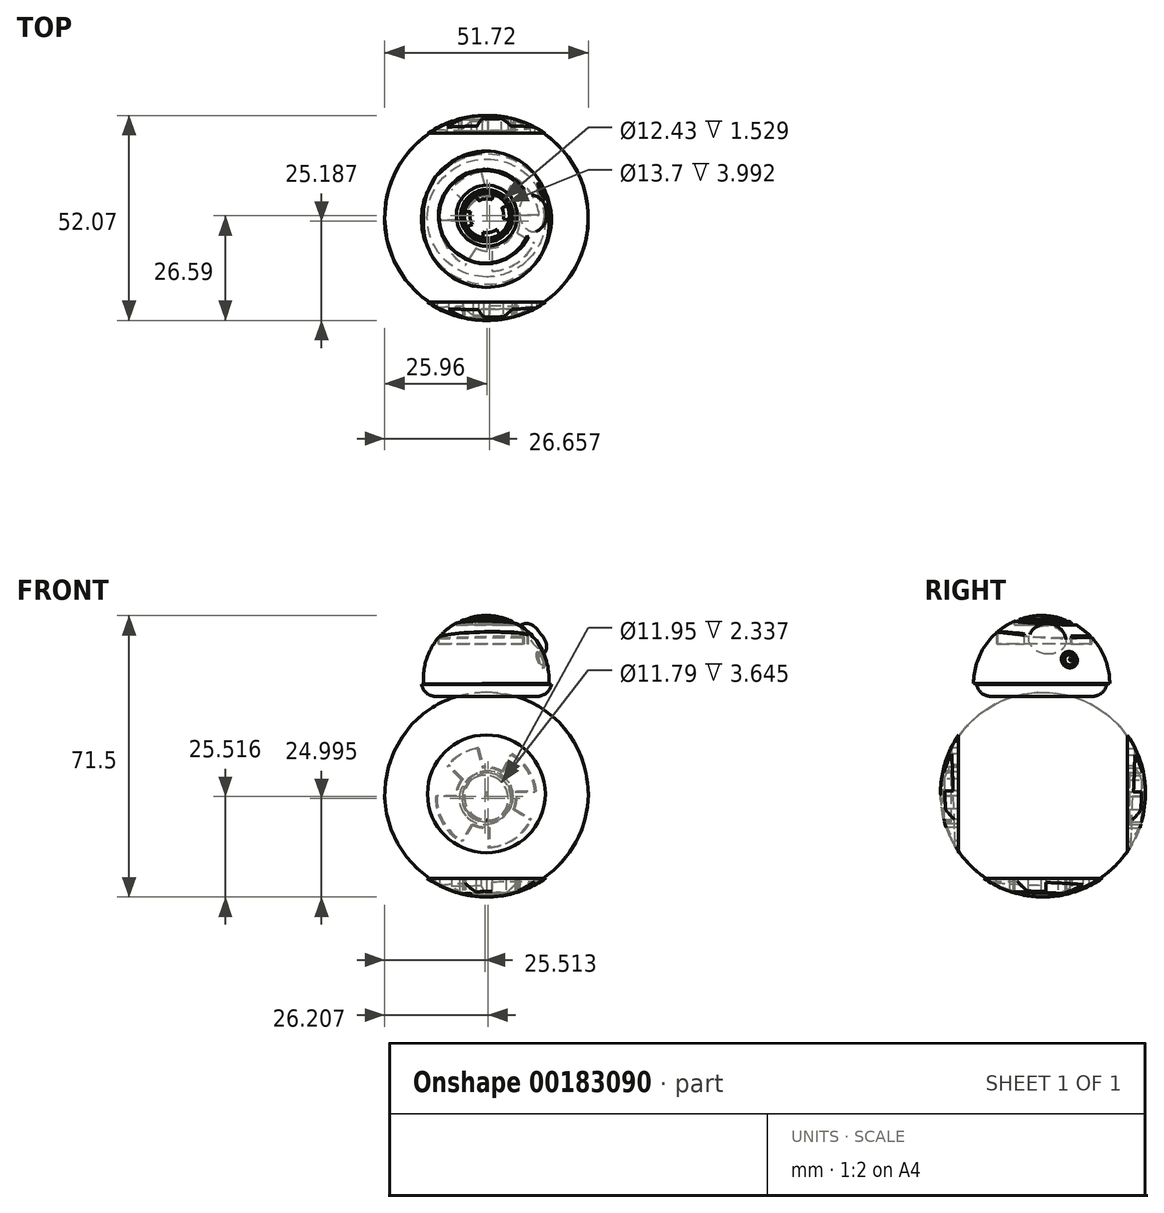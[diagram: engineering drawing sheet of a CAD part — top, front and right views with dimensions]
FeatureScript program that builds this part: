
annotation { "Feature Type Name" : "Feature", "Feature Type Description" : "" }
export const myFeature = defineFeature(function(context is Context, id is Id, definition is map)
    precondition{}
    {
        {
            var Q0;
            Q0=qCreatedBy(makeId("Right.planeOp"),FACE);
            var sketch = newSketch(context, id + "F0", { "sketchPlane" : qUnion([Q0])});
            skArc(sketch, "E0", {"start": v(-25.69, 0) * mm, "mid": v(0.35, -26.2) * mm, "end": v(26.38, 0) * mm});
            skLineSegment(sketch, "E1", {"start": v(-25.69, 0) * mm, "end": v(26.38, 0) * mm});
            skSolve(sketch);
        }
        {
            var Q0;
            Q0=makeQuery(id+"F0.imprint","IMPRINT",FACE,{"disambiguationData":[TD([[makeQuery(id+"F0.imprint","IMPRINT",EDGE,{"derivedFrom":sQuery(id+"F0.wireOp",EDGE,"E0")}),1.0]])]});
            var Q1;
            Q1=sQuery(id+"F0.wireOp",EDGE,"E1");
            revolve(context, id + "F1", {"entities" : qUnion([Q0]), "axis" : qUnion([Q1]), "revolveType" : RevolveType.FULL});
        }
        {
            var Q0;
            Q0=qCreatedBy(makeId("Top.planeOp"),FACE);
            cPlane(context, id + "F2", {"entities" : qUnion([Q0]), "cplaneType" : CPlaneType.OFFSET, "offset" : 26.03 * mm, "width" : 152.4 * mm, "height" : 152.4 * mm});
        }
        {
            var Q0;
            Q0=qCreatedBy(id+"F2.planeOp",FACE);
            cPlane(context, id + "F3", {"entities" : qUnion([Q0]), "cplaneType" : CPlaneType.OFFSET, "offset" : 1.78 * mm, "width" : 152.4 * mm, "height" : 152.4 * mm});
        }
        {
            var Q0;
            Q0=qCreatedBy(id+"F3.planeOp",FACE);
            var sketch = newSketch(context, id + "F4", { "sketchPlane" : qUnion([Q0])});
            skCircle(sketch, "E2", {"center": v(0, 0) * mm, "radius": 16.51 * mm});
            skSolve(sketch);
        }
        {
            var Q0;
            Q0=makeQuery(id+"F4.imprint","IMPRINT",FACE,{"disambiguationData":[TD([[makeQuery(id+"F4.imprint","IMPRINT",EDGE,{"derivedFrom":sQuery(id+"F4.wireOp",EDGE,"E2")}),1.0]])]});
            extrude(context, id + "F5", {"entities" : qUnion([Q0]), "oppositeDirection" : true, "depth" : 3.05 * mm});
        }
        {
            var Q0;
            Q0=makeQuery(id+"F5.opExtrude","CAP_EDGE",EDGE,{"disambiguationData":[OSD([sQuery(id+"F4.wireOp",EDGE,"E2")])],"isStart":false});
            fillet(context, id + "F6", {"entities" : qUnion([Q0]), "radius" : 3.68 * mm, "tangentPropagation" : true, "allowEdgeOverflow" : false});
        }
        {
            var Q0;
            Q0=qCreatedBy(makeId("Front.planeOp"),FACE);
            var sketch = newSketch(context, id + "F7", { "sketchPlane" : qUnion([Q0])});
            skArc(sketch, "E3", {"start": v(15.81, 28.1) * mm, "mid": v(-0.17, 45.29) * mm, "end": v(-15.94, 27.89) * mm});
            skLineSegment(sketch, "E4", {"start": v(-15.94, 27.89) * mm, "end": v(15.81, 28.1) * mm});
            skSolve(sketch);
        }
        {
            var Q0;
            Q0=makeQuery(id+"F7.imprint","IMPRINT",FACE,{"disambiguationData":[TD([[makeQuery(id+"F7.imprint","IMPRINT",EDGE,{"derivedFrom":sQuery(id+"F7.wireOp",EDGE,"E3")}),1.0]])]});
            var Q1;
            Q1=sQuery(id+"F7.wireOp",EDGE,"E4");
            revolve(context, id + "F8", {"operationType" : NewBodyOperationType.ADD, "entities" : qUnion([Q0]), "axis" : qUnion([Q1]), "revolveType" : RevolveType.SYMMETRIC, "angle" : 180 * degree});
        }
        {
            var Q0;
            Q0=qCreatedBy(id+"F3.planeOp",FACE);
            var sketch = newSketch(context, id + "F9", { "sketchPlane" : qUnion([Q0])});
            skPoint(sketch, "E5", {"position": v(21.38, 0) * mm});
            skSolve(sketch);
        }
        {
            var Q0;
            Q0=qCreatedBy(makeId("Right.planeOp"),FACE);
            var sketch = newSketch(context, id + "F10", { "sketchPlane" : qUnion([Q0])});
            skPoint(sketch, "E6", {"position": v(0, 55.63) * mm});
            skSolve(sketch);
        }
        {
            var Q0;
            Q0=qCreatedBy(id+"F3.planeOp",FACE);
            var sketch = newSketch(context, id + "F11", { "sketchPlane" : qUnion([Q0])});
            skPoint(sketch, "E7", {"position": v(20.32, 18.91) * mm});
            skSolve(sketch);
        }
        {
            var Q0;
            Q0=sQuery(id+"F10.wireOp",VERTEX,"E6");
            var Q1;
            Q1=sQuery(id+"F11.wireOp",VERTEX,"E7");
            var Q2;
            Q2=sQuery(id+"F9.wireOp",VERTEX,"E5");
            cPlane(context, id + "F12", {"entities" : qUnion([Q0, Q1, Q2]), "cplaneType" : CPlaneType.THREE_POINT, "offset" : 25.4 * mm, "width" : 152.4 * mm, "height" : 152.4 * mm});
        }
        {
            var Q0;
            Q0=qCreatedBy(id+"F12.planeOp",FACE);
            var sketch = newSketch(context, id + "F13", { "sketchPlane" : qUnion([Q0])});
            skCircle(sketch, "E8", {"center": v(0, 24) * mm, "radius": 4.74 * mm});
            skSolve(sketch);
        }
        {
            var Q0;
            Q0=makeQuery(id+"F13.imprint","IMPRINT",FACE,{"disambiguationData":[TD([[makeQuery(id+"F13.imprint","IMPRINT",EDGE,{"derivedFrom":sQuery(id+"F13.wireOp",EDGE,"E8")}),1.0]])]});
            var Q1;
            Q1=makeQuery(id+"F8.opRevolve","SWEPT_FACE",FACE,{"disambiguationData":[OSD([sQuery(id+"F7.wireOp",EDGE,"E3")])]});
            extrude(context, id + "F14", {"entities" : qUnion([Q0]), "depth" : 1.78 * mm, "hasSecondDirection" : true, "secondDirectionBound" : SecondDirectionBoundingType.UP_TO_SURFACE, "secondDirectionOppositeDirection" : true, "secondDirectionBoundEntityFace" : qUnion([Q1]), "secondDirectionDepth" : 5.08 * mm});
        }
        {
            var Q0;
            {var subQ0=sQuery(id+"F13.wireOp",EDGE,"E8");Q0=makeQuery(id+"F14.opExtrude","CAP_EDGE",EDGE,{"disambiguationData":[OSD([subQ0]),topologyDisambiguationEdgeConnected([makeQuery(id+"F13.imprint","IMPRINT",EDGE,{"derivedFrom":subQ0})])],"isStart":false});}
            fillet(context, id + "F15", {"entities" : qUnion([Q0]), "radius" : 3.07 * mm, "tangentPropagation" : true, "allowEdgeOverflow" : false});
        }
        {
            var Q0;
            Q0=qCreatedBy(id+"F2.planeOp",FACE);
            var sketch = newSketch(context, id + "F16", { "sketchPlane" : qUnion([Q0])});
            skPoint(sketch, "E9", {"position": v(10.76, 18.4) * mm});
            skPoint(sketch, "E10", {"position": v(18.92, 0.35) * mm});
            skSolve(sketch);
        }
        {
            var Q0;
            Q0=qCreatedBy(makeId("Right.planeOp"),FACE);
            var sketch = newSketch(context, id + "F17", { "sketchPlane" : qUnion([Q0])});
            skPoint(sketch, "E11", {"position": v(18.3, 75.37) * mm});
            skSolve(sketch);
        }
        {
            var Q0;
            Q0=sQuery(id+"F17.wireOp",VERTEX,"E11");
            var Q1;
            Q1=sQuery(id+"F16.wireOp",VERTEX,"E10");
            var Q2;
            Q2=sQuery(id+"F16.wireOp",VERTEX,"E9");
            cPlane(context, id + "F18", {"entities" : qUnion([Q0, Q1, Q2]), "cplaneType" : CPlaneType.THREE_POINT, "offset" : 25.4 * mm, "width" : 152.4 * mm, "height" : 152.4 * mm});
        }
        {
            var Q0;
            Q0=qCreatedBy(id+"F18.planeOp",FACE);
            var sketch = newSketch(context, id + "F19", { "sketchPlane" : qUnion([Q0])});
            skCircle(sketch, "E12", {"center": v(1.97, 30.3) * mm, "radius": 2.1 * mm});
            skCircle(sketch, "E13", {"center": v(1.97, 30.3) * mm, "radius": 1.85 * mm});
            skSolve(sketch);
        }
        {
            var Q0;
            Q0=makeQuery(id+"F19.imprint","IMPRINT",FACE,{"disambiguationData":[TD([[makeQuery(id+"F19.imprint","IMPRINT",EDGE,{"derivedFrom":sQuery(id+"F19.wireOp",EDGE,"E12")}),1.0]])]});
            var Q1;
            Q1=makeQuery(id+"F8.opRevolve","SWEPT_FACE",FACE,{"disambiguationData":[OSD([sQuery(id+"F7.wireOp",EDGE,"E3")])]});
            extrude(context, id + "F20", {"entities" : qUnion([Q0]), "endBound" : BoundingType.UP_TO_SURFACE, "endBoundEntityFace" : qUnion([Q1]), "depth" : 25.4 * mm});
        }
        {
            var Q0;
            Q0=qCreatedBy(id+"F18.planeOp",FACE);
            var sketch = newSketch(context, id + "F21", { "sketchPlane" : qUnion([Q0])});
            skCircle(sketch, "E14", {"center": v(1.9, 30.29) * mm, "radius": 1.29 * mm});
            skSolve(sketch);
        }
        {
            var Q0;
            Q0=makeQuery(id+"F21.imprint","IMPRINT",FACE,{"disambiguationData":[TD([[makeQuery(id+"F21.imprint","IMPRINT",EDGE,{"derivedFrom":sQuery(id+"F21.wireOp",EDGE,"E14")}),1.0]])]});
            var Q1;
            Q1=makeQuery(id+"F8.opRevolve","SWEPT_FACE",FACE,{"disambiguationData":[OSD([sQuery(id+"F7.wireOp",EDGE,"E3")])]});
            extrude(context, id + "F22", {"entities" : qUnion([Q0]), "operationType" : NewBodyOperationType.ADD, "oppositeDirection" : true, "depth" : 0.38 * mm, "hasSecondDirection" : true, "secondDirectionBound" : SecondDirectionBoundingType.UP_TO_SURFACE, "secondDirectionOppositeDirection" : false, "secondDirectionBoundEntityFace" : qUnion([Q1]), "secondDirectionDepth" : 25.4 * mm});
        }
        {
            var Q0;
            {var subQ0=sQuery(id+"F21.wireOp",EDGE,"E14");Q0=makeQuery(id+"F22.opExtrude","CAP_EDGE",EDGE,{"disambiguationData":[OSD([subQ0]),topologyDisambiguationEdgeConnected([makeQuery(id+"F21.imprint","IMPRINT",EDGE,{"derivedFrom":subQ0})])],"isStart":false});}
            fillet(context, id + "F23", {"entities" : qUnion([Q0]), "radius" : 0.98 * mm, "tangentPropagation" : true, "allowEdgeOverflow" : false});
        }
        {
            var Q0;
            Q0=qCreatedBy(makeId("Top.planeOp"),FACE);
            var sketch = newSketch(context, id + "F24", { "sketchPlane" : qUnion([Q0])});
            skPoint(sketch, "E15", {"position": v(32.89, -76.08) * mm});
            skPoint(sketch, "E16", {"position": v(27.47, -77.7) * mm});
            skPoint(sketch, "E17", {"position": v(27.47, 37.08) * mm});
            skSolve(sketch);
        }
        {
            var Q0;
            Q0=sQuery(id+"F24.wireOp",VERTEX,"E15");
            var Q1;
            Q1=sQuery(id+"F24.wireOp",VERTEX,"E17");
            var Q2;
            Q2=sQuery(id+"F17.wireOp",VERTEX,"E11");
            cPlane(context, id + "F25", {"entities" : qUnion([Q0, Q1, Q2]), "cplaneType" : CPlaneType.THREE_POINT, "offset" : 25.4 * mm, "width" : 152.4 * mm, "height" : 152.4 * mm});
        }
        {
            var Q0;
            Q0=sQuery(id+"F24.wireOp",VERTEX,"E17");
            var Q1;
            Q1=sQuery(id+"F24.wireOp",VERTEX,"E15");
            var Q2;
            Q2=sQuery(id+"F17.wireOp",VERTEX,"E11");
            cPlane(context, id + "F26", {"entities" : qUnion([Q0, Q1, Q2]), "cplaneType" : CPlaneType.THREE_POINT, "offset" : 25.4 * mm, "width" : 152.4 * mm, "height" : 152.4 * mm});
        }
        {
            var Q0;
            Q0=qCreatedBy(makeId("Right.planeOp"),FACE);
            var sketch = newSketch(context, id + "F27", { "sketchPlane" : qUnion([Q0])});
            skPoint(sketch, "E18", {"position": v(23.46, -62.95) * mm});
            skPoint(sketch, "E19", {"position": v(17.8, 74.84) * mm});
            skSolve(sketch);
        }
        {
            var Q0;
            Q0=sQuery(id+"F27.wireOp",VERTEX,"E18");
            var Q1;
            Q1=sQuery(id+"F24.wireOp",VERTEX,"E15");
            var Q2;
            Q2=sQuery(id+"F24.wireOp",VERTEX,"E17");
            cPlane(context, id + "F28", {"entities" : qUnion([Q0, Q1, Q2]), "cplaneType" : CPlaneType.THREE_POINT, "offset" : 25.4 * mm, "width" : 152.4 * mm, "height" : 152.4 * mm});
        }
        {
            var Q0;
            Q0=qCreatedBy(makeId("Right.planeOp"),FACE);
            cPlane(context, id + "F29", {"entities" : qUnion([Q0]), "cplaneType" : CPlaneType.OFFSET, "offset" : 38.1 * mm, "width" : 152.4 * mm, "height" : 152.4 * mm});
        }
        {
            var Q0;
            Q0=qCreatedBy(id+"F29.planeOp",FACE);
            var sketch = newSketch(context, id + "F30", { "sketchPlane" : qUnion([Q0])});
            skCircle(sketch, "E20", {"center": v(0.51, -0.41) * mm, "radius": 12.7 * mm});
            skCircle(sketch, "E21", {"center": v(0.51, -0.41) * mm, "radius": 16.51 * mm});
            skCircle(sketch, "E22", {"center": v(0.51, -0.41) * mm, "radius": 7.65 * mm});
            skLineSegment(sketch, "E23", {"start": v(-1.63, 12.1) * mm, "end": v(-0.29, 7.2) * mm});
            skLineSegment(sketch, "E24", {"start": v(4.63, 6.04) * mm, "end": v(6.94, 10.54) * mm});
            skLineSegment(sketch, "E25", {"start": v(-3, -7.2) * mm, "end": v(-5.66, -11.5) * mm});
            skLineSegment(sketch, "E26", {"start": v(1.14, -8.04) * mm, "end": v(1.14, -13.1) * mm});
            skLineSegment(sketch, "E27", {"start": v(8, 1.14) * mm, "end": v(13.12, 1.14) * mm});
            skLineSegment(sketch, "E28", {"start": v(7.55, -3.41) * mm, "end": v(11.91, -6) * mm});
            skLineSegment(sketch, "E29", {"start": v(-5.6, 4.2) * mm, "end": v(-9.18, 7.8) * mm});
            skLineSegment(sketch, "E30", {"start": v(-7.13, -0.1) * mm, "end": v(-12.18, -0.1) * mm});
            skSolve(sketch);
        }
        {
            var Q0;
            Q0=makeQuery(id+"F30.imprint","IMPRINT",FACE,{"disambiguationData":[TD([[makeQuery(id+"F30.imprint","IMPRINT",EDGE,{"derivedFrom":sQuery(id+"F30.wireOp",EDGE,"E20")}),-1.0]])]});
            var Q1;
            {var subQ0=sQuery(id+"F30.wireOp",EDGE,"E23");Q1=makeQuery(id+"F30.imprint","IMPRINT",FACE,{"disambiguationData":[TD([[makeQuery(id+"F30.imprint","IMPRINT",EDGE,{"derivedFrom":subQ0}),1.0]])]});}
            var Q2;
            {var subQ0=sQuery(id+"F30.wireOp",EDGE,"E29");Q2=makeQuery(id+"F30.imprint","IMPRINT",FACE,{"disambiguationData":[TD([[makeQuery(id+"F30.imprint","IMPRINT",EDGE,{"derivedFrom":subQ0}),1.0]])]});}
            var Q3;
            {var subQ0=sQuery(id+"F30.wireOp",EDGE,"E27");Q3=makeQuery(id+"F30.imprint","IMPRINT",FACE,{"disambiguationData":[TD([[makeQuery(id+"F30.imprint","IMPRINT",EDGE,{"derivedFrom":subQ0}),-1.0]])]});}
            var Q4;
            {var subQ0=sQuery(id+"F30.wireOp",EDGE,"E25");Q4=makeQuery(id+"F30.imprint","IMPRINT",FACE,{"disambiguationData":[TD([[makeQuery(id+"F30.imprint","IMPRINT",EDGE,{"derivedFrom":subQ0}),1.0]])]});}
            var Q5;
            Q5=sQuery(id+"F30.wireOp",EDGE,"E21");
            var Q6;
            Q6=sQuery(id+"F30.wireOp",EDGE,"E20");
            extrude(context, id + "F31", {"entities" : qUnion([Q0, Q1, Q2, Q3, Q4]), "operationType" : NewBodyOperationType.REMOVE, "surfaceEntities" : qUnion([Q5, Q6]), "oppositeDirection" : true, "depth" : 16.5 * mm});
        }
        {
            var Q0;
            Q0=qCreatedBy(makeId("Right.planeOp"),FACE);
            cPlane(context, id + "F32", {"entities" : qUnion([Q0]), "cplaneType" : CPlaneType.OFFSET, "offset" : 30.48 * mm, "width" : 152.4 * mm, "height" : 152.4 * mm});
        }
        {
            var Q0;
            Q0=qCreatedBy(id+"F32.planeOp",FACE);
            var sketch = newSketch(context, id + "F33", { "sketchPlane" : qUnion([Q0])});
            skCircle(sketch, "E31", {"center": v(0.35, -0.52) * mm, "radius": 6.22 * mm});
            skCircle(sketch, "E32", {"center": v(0.35, -0.52) * mm, "radius": 5.81 * mm});
            skSolve(sketch);
        }
        {
            var Q0;
            Q0=makeQuery(id+"F33.imprint","IMPRINT",FACE,{"disambiguationData":[TD([[makeQuery(id+"F33.imprint","IMPRINT",EDGE,{"derivedFrom":sQuery(id+"F33.wireOp",EDGE,"E31")}),1.0]])]});
            extrude(context, id + "F34", {"entities" : qUnion([Q0]), "operationType" : NewBodyOperationType.REMOVE, "oppositeDirection" : true, "depth" : 7.62 * mm});
        }
        {
            var Q0;
            Q0=qCreatedBy(makeId("Top.planeOp"),FACE);
            cPlane(context, id + "F35", {"entities" : qUnion([Q0]), "cplaneType" : CPlaneType.OFFSET, "offset" : 50.8 * mm, "width" : 152.4 * mm, "height" : 152.4 * mm});
        }
        {
            var Q0;
            Q0=qCreatedBy(id+"F35.planeOp",FACE);
            var sketch = newSketch(context, id + "F36", { "sketchPlane" : qUnion([Q0])});
            skCircle(sketch, "E33", {"center": v(0.1, 0.9) * mm, "radius": 7.77 * mm});
            skCircle(sketch, "E34", {"center": v(0.1, 0.9) * mm, "radius": 6.64 * mm});
            skCircle(sketch, "E35", {"center": v(0.1, 0.9) * mm, "radius": 6.21 * mm});
            skCircle(sketch, "E36", {"center": v(0.1, 0.9) * mm, "radius": 4.3 * mm});
            skCircle(sketch, "E37", {"center": v(0.1, 0.9) * mm, "radius": 5.7 * mm});
            skLineSegment(sketch, "E38", {"start": v(3.91, 2.89) * mm, "end": v(5.21, 3.43) * mm});
            skLineSegment(sketch, "E39", {"start": v(4.27, -0.14) * mm, "end": v(5.71, -0.14) * mm});
            skLineSegment(sketch, "E40", {"start": v(2.6, -2.6) * mm, "end": v(3.3, -3.82) * mm});
            skLineSegment(sketch, "E41", {"start": v(-3.57, -1.33) * mm, "end": v(-4.9, -1.85) * mm});
            skLineSegment(sketch, "E42", {"start": v(-0.88, -3.28) * mm, "end": v(-0.88, -4.72) * mm});
            skLineSegment(sketch, "E43", {"start": v(-5.5, 1.95) * mm, "end": v(-4.07, 1.95) * mm});
            skLineSegment(sketch, "E44", {"start": v(-2.78, 5.82) * mm, "end": v(-1.95, 4.68) * mm});
            skLineSegment(sketch, "E45", {"start": v(1.37, 5) * mm, "end": v(1.84, 6.33) * mm});
            skArc(sketch, "E46", {"start": v(9.61, 7.65) * mm, "mid": v(-12.17, -0.39) * mm, "end": v(10.7, -4.36) * mm});
            skLineSegment(sketch, "E47", {"start": v(9.61, 7.65) * mm, "end": v(9.3, 7.46) * mm});
            skLineSegment(sketch, "E48", {"start": v(10.7, -4.36) * mm, "end": v(10.37, -4.33) * mm});
            skArc(sketch, "E49", {"start": v(9.3, 7.46) * mm, "mid": v(-12.04, -0.42) * mm, "end": v(10.37, -4.33) * mm});
            skSolve(sketch);
        }
        {
            var Q0;
            Q0=makeQuery(id+"F36.imprint","IMPRINT",FACE,{"disambiguationData":[TD([[makeQuery(id+"F36.imprint","IMPRINT",EDGE,{"derivedFrom":sQuery(id+"F36.wireOp",EDGE,"E33")}),1.0]])]});
            var Q1;
            Q1=makeQuery(id+"F36.imprint","IMPRINT",FACE,{"disambiguationData":[TD([[makeQuery(id+"F36.imprint","IMPRINT",EDGE,{"derivedFrom":sQuery(id+"F36.wireOp",EDGE,"E35")}),1.0]])]});
            extrude(context, id + "F37", {"entities" : qUnion([Q0, Q1]), "operationType" : NewBodyOperationType.REMOVE, "oppositeDirection" : true, "depth" : 7.87 * mm});
        }
        {
            var Q0;
            Q0=qCreatedBy(makeId("Right.planeOp"),FACE);
            cPlane(context, id + "F38", {"entities" : qUnion([Q0]), "cplaneType" : CPlaneType.OFFSET, "offset" : 33.02 * mm, "oppositeDirection" : true, "width" : 152.4 * mm, "height" : 152.4 * mm});
        }
        {
            var Q0;
            Q0=qCreatedBy(id+"F38.planeOp",FACE);
            var sketch = newSketch(context, id + "F39", { "sketchPlane" : qUnion([Q0])});
            skCircle(sketch, "E50", {"center": v(0.47, -0.65) * mm, "radius": 12.7 * mm});
            skCircle(sketch, "E51", {"center": v(0.47, -0.65) * mm, "radius": 16.51 * mm});
            skCircle(sketch, "E52", {"center": v(0.47, -0.65) * mm, "radius": 7.65 * mm});
            skLineSegment(sketch, "E53", {"start": v(-1.67, 11.87) * mm, "end": v(-0.33, 6.96) * mm});
            skLineSegment(sketch, "E54", {"start": v(4.59, 5.8) * mm, "end": v(6.9, 10.3) * mm});
            skLineSegment(sketch, "E55", {"start": v(-3.04, -7.45) * mm, "end": v(-5.7, -11.75) * mm});
            skLineSegment(sketch, "E56", {"start": v(1.1, -8.27) * mm, "end": v(1.1, -13.33) * mm});
            skLineSegment(sketch, "E57", {"start": v(7.96, 0.9) * mm, "end": v(13.07, 0.9) * mm});
            skLineSegment(sketch, "E58", {"start": v(7.5, -3.65) * mm, "end": v(11.87, -6.24) * mm});
            skLineSegment(sketch, "E59", {"start": v(-5.64, 3.95) * mm, "end": v(-9.23, 7.55) * mm});
            skLineSegment(sketch, "E60", {"start": v(-7.17, -0.34) * mm, "end": v(-12.23, -0.34) * mm});
            skSolve(sketch);
        }
        {
            var Q0;
            Q0=makeQuery(id+"F39.imprint","IMPRINT",FACE,{"disambiguationData":[TD([[makeQuery(id+"F39.imprint","IMPRINT",EDGE,{"derivedFrom":sQuery(id+"F39.wireOp",EDGE,"E51")}),1.0]])]});
            var Q1;
            {var subQ0=sQuery(id+"F39.wireOp",EDGE,"E53");Q1=makeQuery(id+"F39.imprint","IMPRINT",FACE,{"disambiguationData":[TD([[makeQuery(id+"F39.imprint","IMPRINT",EDGE,{"derivedFrom":subQ0}),1.0]])]});}
            var Q2;
            {var subQ0=sQuery(id+"F39.wireOp",EDGE,"E59");Q2=makeQuery(id+"F39.imprint","IMPRINT",FACE,{"disambiguationData":[TD([[makeQuery(id+"F39.imprint","IMPRINT",EDGE,{"derivedFrom":subQ0}),1.0]])]});}
            var Q3;
            {var subQ0=sQuery(id+"F39.wireOp",EDGE,"E55");Q3=makeQuery(id+"F39.imprint","IMPRINT",FACE,{"disambiguationData":[TD([[makeQuery(id+"F39.imprint","IMPRINT",EDGE,{"derivedFrom":subQ0}),1.0]])]});}
            var Q4;
            {var subQ0=sQuery(id+"F39.wireOp",EDGE,"E57");Q4=makeQuery(id+"F39.imprint","IMPRINT",FACE,{"disambiguationData":[TD([[makeQuery(id+"F39.imprint","IMPRINT",EDGE,{"derivedFrom":subQ0}),-1.0]])]});}
            extrude(context, id + "F40", {"entities" : qUnion([Q0, Q1, Q2, Q3, Q4]), "operationType" : NewBodyOperationType.REMOVE, "depth" : 11.43 * mm});
        }
        {
            var Q0;
            Q0=qCreatedBy(makeId("Front.planeOp"),FACE);
            cPlane(context, id + "F41", {"entities" : qUnion([Q0]), "cplaneType" : CPlaneType.OFFSET, "offset" : 38.1 * mm, "width" : 152.4 * mm, "height" : 152.4 * mm});
        }
        {
            var Q0;
            Q0=qCreatedBy(makeId("Front.planeOp"),FACE);
            cPlane(context, id + "F42", {"entities" : qUnion([Q0]), "cplaneType" : CPlaneType.OFFSET, "offset" : 38.1 * mm, "oppositeDirection" : true, "width" : 152.4 * mm, "height" : 152.4 * mm});
        }
        {
            var Q0;
            Q0=qCreatedBy(id+"F42.planeOp",FACE);
            var sketch = newSketch(context, id + "F43", { "sketchPlane" : qUnion([Q0])});
            skCircle(sketch, "E61", {"center": v(-0.24, -1.02) * mm, "radius": 12.7 * mm});
            skCircle(sketch, "E62", {"center": v(-0.24, -1.02) * mm, "radius": 16.51 * mm});
            skCircle(sketch, "E63", {"center": v(-0.24, -1.02) * mm, "radius": 7.65 * mm});
            skLineSegment(sketch, "E64", {"start": v(-2.38, 11.5) * mm, "end": v(-1.04, 6.58) * mm});
            skLineSegment(sketch, "E65", {"start": v(3.87, 5.42) * mm, "end": v(6.18, 9.93) * mm});
            skLineSegment(sketch, "E66", {"start": v(-3.75, -7.82) * mm, "end": v(-6.42, -12.12) * mm});
            skLineSegment(sketch, "E67", {"start": v(0.38, -8.65) * mm, "end": v(0.38, -13.7) * mm});
            skLineSegment(sketch, "E68", {"start": v(7.25, 0.53) * mm, "end": v(12.36, 0.53) * mm});
            skLineSegment(sketch, "E69", {"start": v(6.8, -4.03) * mm, "end": v(11.16, -6.62) * mm});
            skLineSegment(sketch, "E70", {"start": v(-6.36, 3.58) * mm, "end": v(-9.94, 7.18) * mm});
            skLineSegment(sketch, "E71", {"start": v(-7.89, -0.71) * mm, "end": v(-12.94, -0.71) * mm});
            skSolve(sketch);
        }
        {
            var Q0;
            Q0=qCreatedBy(id+"F41.planeOp",FACE);
            var sketch = newSketch(context, id + "F44", { "sketchPlane" : qUnion([Q0])});
            skCircle(sketch, "E72", {"center": v(0.1, -0.85) * mm, "radius": 12.7 * mm});
            skCircle(sketch, "E73", {"center": v(0.1, -0.85) * mm, "radius": 16.51 * mm});
            skCircle(sketch, "E74", {"center": v(0.1, -0.85) * mm, "radius": 7.65 * mm});
            skLineSegment(sketch, "E75", {"start": v(-2.04, 11.67) * mm, "end": v(-0.7, 6.76) * mm});
            skLineSegment(sketch, "E76", {"start": v(4.22, 5.6) * mm, "end": v(6.53, 10.1) * mm});
            skLineSegment(sketch, "E77", {"start": v(-3.4, -7.65) * mm, "end": v(-6.07, -11.95) * mm});
            skLineSegment(sketch, "E78", {"start": v(0.73, -8.48) * mm, "end": v(0.73, -13.53) * mm});
            skLineSegment(sketch, "E79", {"start": v(7.6, 0.7) * mm, "end": v(12.7, 0.7) * mm});
            skLineSegment(sketch, "E80", {"start": v(7.14, -3.85) * mm, "end": v(11.5, -6.44) * mm});
            skLineSegment(sketch, "E81", {"start": v(-6, 3.75) * mm, "end": v(-9.6, 7.35) * mm});
            skLineSegment(sketch, "E82", {"start": v(-7.54, -0.54) * mm, "end": v(-12.6, -0.54) * mm});
            skSolve(sketch);
        }
        {
            var Q0;
            Q0=makeQuery(id+"F44.imprint","IMPRINT",FACE,{"disambiguationData":[TD([[makeQuery(id+"F44.imprint","IMPRINT",EDGE,{"derivedFrom":sQuery(id+"F44.wireOp",EDGE,"E73")}),1.0]])]});
            var Q1;
            {var subQ0=sQuery(id+"F44.wireOp",EDGE,"E75");Q1=makeQuery(id+"F44.imprint","IMPRINT",FACE,{"disambiguationData":[TD([[makeQuery(id+"F44.imprint","IMPRINT",EDGE,{"derivedFrom":subQ0}),1.0]])]});}
            var Q2;
            {var subQ0=sQuery(id+"F44.wireOp",EDGE,"E81");Q2=makeQuery(id+"F44.imprint","IMPRINT",FACE,{"disambiguationData":[TD([[makeQuery(id+"F44.imprint","IMPRINT",EDGE,{"derivedFrom":subQ0}),1.0]])]});}
            var Q3;
            {var subQ0=sQuery(id+"F44.wireOp",EDGE,"E79");Q3=makeQuery(id+"F44.imprint","IMPRINT",FACE,{"disambiguationData":[TD([[makeQuery(id+"F44.imprint","IMPRINT",EDGE,{"derivedFrom":subQ0}),-1.0]])]});}
            var Q4;
            {var subQ0=sQuery(id+"F44.wireOp",EDGE,"E77");Q4=makeQuery(id+"F44.imprint","IMPRINT",FACE,{"disambiguationData":[TD([[makeQuery(id+"F44.imprint","IMPRINT",EDGE,{"derivedFrom":subQ0}),1.0]])]});}
            extrude(context, id + "F45", {"entities" : qUnion([Q0, Q1, Q2, Q3, Q4]), "operationType" : NewBodyOperationType.REMOVE, "oppositeDirection" : true, "depth" : 17.02 * mm});
        }
        {
            var Q0;
            Q0=makeQuery(id+"F43.imprint","IMPRINT",FACE,{"disambiguationData":[TD([[makeQuery(id+"F43.imprint","IMPRINT",EDGE,{"derivedFrom":sQuery(id+"F43.wireOp",EDGE,"E62")}),1.0]])]});
            var Q1;
            {var subQ0=sQuery(id+"F43.wireOp",EDGE,"E66");Q1=makeQuery(id+"F43.imprint","IMPRINT",FACE,{"disambiguationData":[TD([[makeQuery(id+"F43.imprint","IMPRINT",EDGE,{"derivedFrom":subQ0}),1.0]])]});}
            var Q2;
            {var subQ0=sQuery(id+"F43.wireOp",EDGE,"E68");Q2=makeQuery(id+"F43.imprint","IMPRINT",FACE,{"disambiguationData":[TD([[makeQuery(id+"F43.imprint","IMPRINT",EDGE,{"derivedFrom":subQ0}),-1.0]])]});}
            var Q3;
            {var subQ0=sQuery(id+"F43.wireOp",EDGE,"E64");Q3=makeQuery(id+"F43.imprint","IMPRINT",FACE,{"disambiguationData":[TD([[makeQuery(id+"F43.imprint","IMPRINT",EDGE,{"derivedFrom":subQ0}),1.0]])]});}
            var Q4;
            {var subQ0=sQuery(id+"F43.wireOp",EDGE,"E70");Q4=makeQuery(id+"F43.imprint","IMPRINT",FACE,{"disambiguationData":[TD([[makeQuery(id+"F43.imprint","IMPRINT",EDGE,{"derivedFrom":subQ0}),1.0]])]});}
            extrude(context, id + "F46", {"entities" : qUnion([Q0, Q1, Q2, Q3, Q4]), "operationType" : NewBodyOperationType.REMOVE, "depth" : 16.26 * mm});
        }
        {
            var Q0;
            Q0=qCreatedBy(id+"F41.planeOp",FACE);
            var sketch = newSketch(context, id + "F47", { "sketchPlane" : qUnion([Q0])});
            skCircle(sketch, "E83", {"center": v(0.35, -0.7) * mm, "radius": 6.48 * mm});
            skCircle(sketch, "E84", {"center": v(0.35, -0.7) * mm, "radius": 5.98 * mm});
            skSolve(sketch);
        }
        {
            var Q0;
            Q0=makeQuery(id+"F47.imprint","IMPRINT",FACE,{"disambiguationData":[TD([[makeQuery(id+"F47.imprint","IMPRINT",EDGE,{"derivedFrom":sQuery(id+"F47.wireOp",EDGE,"E83")}),1.0]])]});
            extrude(context, id + "F48", {"entities" : qUnion([Q0]), "operationType" : NewBodyOperationType.REMOVE, "oppositeDirection" : true, "depth" : 15.24 * mm});
        }
        {
            var Q0;
            Q0=qCreatedBy(id+"F42.planeOp",FACE);
            var sketch = newSketch(context, id + "F49", { "sketchPlane" : qUnion([Q0])});
            skCircle(sketch, "E85", {"center": v(-0.35, -1.21) * mm, "radius": 6.58 * mm});
            skCircle(sketch, "E86", {"center": v(-0.35, -1.21) * mm, "radius": 5.9 * mm});
            skSolve(sketch);
        }
        {
            var Q0;
            Q0=makeQuery(id+"F49.imprint","IMPRINT",FACE,{"disambiguationData":[TD([[makeQuery(id+"F49.imprint","IMPRINT",EDGE,{"derivedFrom":sQuery(id+"F49.wireOp",EDGE,"E85")}),1.0]])]});
            extrude(context, id + "F50", {"entities" : qUnion([Q0]), "operationType" : NewBodyOperationType.REMOVE, "depth" : 15.75 * mm});
        }
        {
            var Q0;
            Q0=qCreatedBy(id+"F38.planeOp",FACE);
            var sketch = newSketch(context, id + "F51", { "sketchPlane" : qUnion([Q0])});
            skCircle(sketch, "E87", {"center": v(0.43, -0.7) * mm, "radius": 6.76 * mm});
            skCircle(sketch, "E88", {"center": v(0.43, -0.7) * mm, "radius": 6.28 * mm});
            skSolve(sketch);
        }
        {
            var Q0;
            Q0=makeQuery(id+"F51.imprint","IMPRINT",FACE,{"disambiguationData":[TD([[makeQuery(id+"F51.imprint","IMPRINT",EDGE,{"derivedFrom":sQuery(id+"F51.wireOp",EDGE,"E87")}),1.0]])]});
            extrude(context, id + "F52", {"entities" : qUnion([Q0]), "operationType" : NewBodyOperationType.REMOVE, "depth" : 12.7 * mm});
        }
        {
            var Q0;
            Q0=qCreatedBy(makeId("Top.planeOp"),FACE);
            cPlane(context, id + "F53", {"entities" : qUnion([Q0]), "cplaneType" : CPlaneType.OFFSET, "offset" : 38.1 * mm, "oppositeDirection" : true, "width" : 152.4 * mm, "height" : 152.4 * mm});
        }
        {
            var Q0;
            Q0=qCreatedBy(id+"F53.planeOp",FACE);
            var sketch = newSketch(context, id + "F54", { "sketchPlane" : qUnion([Q0])});
            skCircle(sketch, "E89", {"center": v(0.8, -0.5) * mm, "radius": 12.7 * mm});
            skCircle(sketch, "E90", {"center": v(0.8, -0.5) * mm, "radius": 16.51 * mm});
            skCircle(sketch, "E91", {"center": v(0.8, -0.5) * mm, "radius": 7.65 * mm});
            skLineSegment(sketch, "E92", {"start": v(-1.34, 12.02) * mm, "end": v(0, 7.1) * mm});
            skLineSegment(sketch, "E93", {"start": v(4.92, 5.94) * mm, "end": v(7.22, 10.45) * mm});
            skLineSegment(sketch, "E94", {"start": v(-2.71, -7.3) * mm, "end": v(-5.38, -11.6) * mm});
            skLineSegment(sketch, "E95", {"start": v(1.42, -8.13) * mm, "end": v(1.42, -13.19) * mm});
            skLineSegment(sketch, "E96", {"start": v(8.29, 1.05) * mm, "end": v(13.4, 1.05) * mm});
            skLineSegment(sketch, "E97", {"start": v(7.83, -3.5) * mm, "end": v(12.2, -6.1) * mm});
            skLineSegment(sketch, "E98", {"start": v(-5.31, 4.1) * mm, "end": v(-8.9, 7.7) * mm});
            skLineSegment(sketch, "E99", {"start": v(-6.85, -0.2) * mm, "end": v(-11.9, -0.2) * mm});
            skCircle(sketch, "E100", {"center": v(0.8, -0.5) * mm, "radius": 6.85 * mm});
            skCircle(sketch, "E101", {"center": v(0.8, -0.5) * mm, "radius": 6.41 * mm});
            skSolve(sketch);
        }
        {
            var Q0;
            {var subQ0=sQuery(id+"F54.wireOp",EDGE,"E94");Q0=makeQuery(id+"F54.imprint","IMPRINT",FACE,{"disambiguationData":[TD([[makeQuery(id+"F54.imprint","IMPRINT",EDGE,{"derivedFrom":subQ0}),1.0]])]});}
            var Q1;
            {var subQ0=sQuery(id+"F54.wireOp",EDGE,"E96");Q1=makeQuery(id+"F54.imprint","IMPRINT",FACE,{"disambiguationData":[TD([[makeQuery(id+"F54.imprint","IMPRINT",EDGE,{"derivedFrom":subQ0}),-1.0]])]});}
            var Q2;
            {var subQ0=sQuery(id+"F54.wireOp",EDGE,"E92");Q2=makeQuery(id+"F54.imprint","IMPRINT",FACE,{"disambiguationData":[TD([[makeQuery(id+"F54.imprint","IMPRINT",EDGE,{"derivedFrom":subQ0}),1.0]])]});}
            var Q3;
            {var subQ0=sQuery(id+"F54.wireOp",EDGE,"E98");Q3=makeQuery(id+"F54.imprint","IMPRINT",FACE,{"disambiguationData":[TD([[makeQuery(id+"F54.imprint","IMPRINT",EDGE,{"derivedFrom":subQ0}),1.0]])]});}
            var Q4;
            Q4=makeQuery(id+"F54.imprint","IMPRINT",FACE,{"disambiguationData":[TD([[makeQuery(id+"F54.imprint","IMPRINT",EDGE,{"derivedFrom":sQuery(id+"F54.wireOp",EDGE,"E90")}),1.0]])]});
            extrude(context, id + "F55", {"entities" : qUnion([Q0, Q1, Q2, Q3, Q4]), "operationType" : NewBodyOperationType.REMOVE, "depth" : 16.64 * mm});
        }
        {
            var Q0;
            Q0=makeQuery(id+"F54.imprint","IMPRINT",FACE,{"disambiguationData":[TD([[makeQuery(id+"F54.imprint","IMPRINT",EDGE,{"derivedFrom":sQuery(id+"F54.wireOp",EDGE,"E100")}),1.0]])]});
            extrude(context, id + "F56", {"entities" : qUnion([Q0]), "operationType" : NewBodyOperationType.REMOVE, "depth" : 16.5 * mm});
        }
        {
            var Q0;
            {var subQ0=sQuery(id+"F36.wireOp",EDGE,"E44");Q0=makeQuery(id+"F36.imprint","IMPRINT",FACE,{"disambiguationData":[TD([[makeQuery(id+"F36.imprint","IMPRINT",EDGE,{"derivedFrom":subQ0}),1.0]])]});}
            var Q1;
            {var subQ0=sQuery(id+"F36.wireOp",EDGE,"E38");Q1=makeQuery(id+"F36.imprint","IMPRINT",FACE,{"disambiguationData":[TD([[makeQuery(id+"F36.imprint","IMPRINT",EDGE,{"derivedFrom":subQ0}),-1.0]])]});}
            var Q2;
            {var subQ0=sQuery(id+"F36.wireOp",EDGE,"E40");Q2=makeQuery(id+"F36.imprint","IMPRINT",FACE,{"disambiguationData":[TD([[makeQuery(id+"F36.imprint","IMPRINT",EDGE,{"derivedFrom":subQ0}),-1.0]])]});}
            var Q3;
            {var subQ0=sQuery(id+"F36.wireOp",EDGE,"E41");Q3=makeQuery(id+"F36.imprint","IMPRINT",FACE,{"disambiguationData":[TD([[makeQuery(id+"F36.imprint","IMPRINT",EDGE,{"derivedFrom":subQ0}),-1.0]])]});}
            var Q4;
            Q4=makeQuery(id+"F36.imprint","IMPRINT",FACE,{"disambiguationData":[TD([[makeQuery(id+"F36.imprint","IMPRINT",EDGE,{"derivedFrom":sQuery(id+"F36.wireOp",EDGE,"E35")}),1.0]])]});
            extrude(context, id + "F57", {"entities" : qUnion([Q0, Q1, Q2, Q3, Q4]), "operationType" : NewBodyOperationType.REMOVE, "oppositeDirection" : true, "depth" : 7.62 * mm});
        }
        {
            var Q0;
            Q0=makeQuery(id+"F36.imprint","IMPRINT",FACE,{"disambiguationData":[TD([[makeQuery(id+"F36.imprint","IMPRINT",EDGE,{"derivedFrom":sQuery(id+"F36.wireOp",EDGE,"E46")}),1.0]])]});
            extrude(context, id + "F58", {"entities" : qUnion([Q0]), "operationType" : NewBodyOperationType.REMOVE, "oppositeDirection" : true, "depth" : 12.7 * mm});
        }
        {
            var Q0;
            Q0=qCreatedBy(makeId("Top.planeOp"),FACE);
            var sketch = newSketch(context, id + "F59", { "sketchPlane" : qUnion([Q0])});
            skPoint(sketch, "E102", {"position": v(32.98, -17.16) * mm});
            skPoint(sketch, "E103", {"position": v(20.4, -30.4) * mm});
            skSolve(sketch);
        }
        {
            var Q0;
            Q0=qCreatedBy(makeId("Front.planeOp"),FACE);
            var sketch = newSketch(context, id + "F60", { "sketchPlane" : qUnion([Q0])});
            skPoint(sketch, "E104", {"position": v(-3.97, 75.73) * mm});
            skSolve(sketch);
        }
        {
            var Q0;
            Q0=sQuery(id+"F59.wireOp",VERTEX,"E102");
            var Q1;
            Q1=sQuery(id+"F59.wireOp",VERTEX,"E103");
            var Q2;
            Q2=sQuery(id+"F60.wireOp",VERTEX,"E104");
            cPlane(context, id + "F61", {"entities" : qUnion([Q0, Q1, Q2]), "cplaneType" : CPlaneType.THREE_POINT, "offset" : 25.4 * mm, "width" : 152.4 * mm, "height" : 152.4 * mm});
        }
    });
